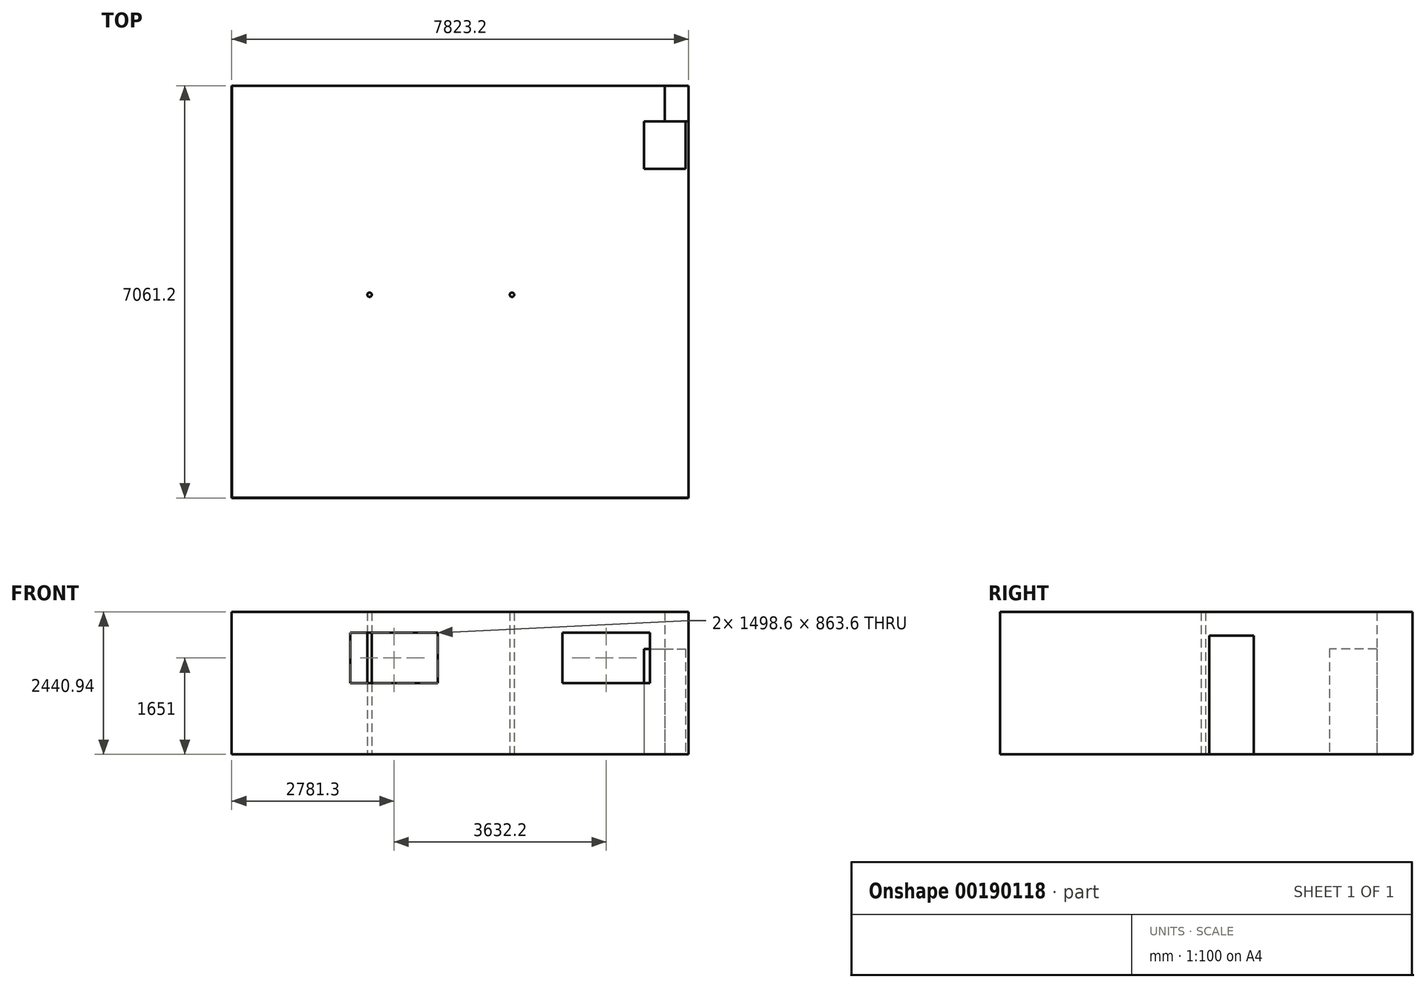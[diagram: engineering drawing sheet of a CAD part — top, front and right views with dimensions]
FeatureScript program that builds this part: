
annotation { "Feature Type Name" : "Feature", "Feature Type Description" : "" }
export const myFeature = defineFeature(function(context is Context, id is Id, definition is map)
    precondition{}
    {
        {
            var Q0;
            Q0=qCreatedBy(makeId("Top.planeOp"),FACE);
            var sketch = newSketch(context, id + "F0", { "sketchPlane" : qUnion([Q0])});
            skLineSegment(sketch, "E0.bottom", {"start": v(-3476.38, 3604.59) * mm, "end": v(4346.82, 3604.59) * mm});
            skLineSegment(sketch, "E0.top", {"start": v(-3476.38, -3456.61) * mm, "end": v(4346.82, -3456.61) * mm});
            skLineSegment(sketch, "E0.left", {"start": v(-3476.38, 3604.59) * mm, "end": v(-3476.38, -3456.61) * mm});
            skLineSegment(sketch, "E0.right", {"start": v(4346.82, 3604.59) * mm, "end": v(4346.82, -3456.61) * mm});
            skSolve(sketch);
        }
        {
            var Q0;
            Q0 = qSketchRegion(id + "F0", true);
            var Q1;
            Q1 = qConstructionFilter(qBodyType(qCreatedBy(id + "F0" ,EDGE), BodyType.WIRE), ConstructionObject.NO);
            extrude(context, id + "F1", {"entities" : qUnion([Q0]), "surfaceEntities" : qUnion([Q1]), "depth" : 2438.4 * mm});
        }
        {
            var Q0;
            Q0=makeQuery(id+"F1.opExtrude","CAP_FACE",FACE,{"disambiguationData":[OSD([sQuery(id+"F0.wireOp",EDGE,"E0.bottom"),sQuery(id+"F0.wireOp",EDGE,"E0.top"),sQuery(id+"F0.wireOp",EDGE,"E0.left"),sQuery(id+"F0.wireOp",EDGE,"E0.right")])],"isStart":false});
            shell(context, id + "F2", {"entities" : qUnion([Q0]), "thickness" : 2.54 * mm});
        }
        {
            var Q0;
            Q0=makeQuery(id+"F1.opExtrude","SWEPT_FACE",FACE,{"disambiguationData":[OSD([sQuery(id+"F0.wireOp",EDGE,"E0.top")])]});
            var sketch = newSketch(context, id + "F3", { "sketchPlane" : qUnion([Q0])});
            skLineSegment(sketch, "E1.bottom", {"start": v(3686.42, 2082.8) * mm, "end": v(2187.82, 2082.8) * mm});
            skLineSegment(sketch, "E1.top", {"start": v(3686.42, 1219.2) * mm, "end": v(2187.82, 1219.2) * mm});
            skLineSegment(sketch, "E1.left", {"start": v(3686.42, 2082.8) * mm, "end": v(3686.42, 1219.2) * mm});
            skLineSegment(sketch, "E1.right", {"start": v(2187.82, 2082.8) * mm, "end": v(2187.82, 1219.2) * mm});
            skLineSegment(sketch, "E2.bottom", {"start": v(54.22, 2082.8) * mm, "end": v(-1444.38, 2082.8) * mm});
            skLineSegment(sketch, "E2.top", {"start": v(54.22, 1219.2) * mm, "end": v(-1444.38, 1219.2) * mm});
            skLineSegment(sketch, "E2.left", {"start": v(54.22, 2082.8) * mm, "end": v(54.22, 1219.2) * mm});
            skLineSegment(sketch, "E2.right", {"start": v(-1444.38, 2082.8) * mm, "end": v(-1444.38, 1219.2) * mm});
            skSolve(sketch);
        }
        {
            var Q0;
            Q0=makeQuery(id+"F3.imprint","IMPRINT",FACE,{"disambiguationData":[TD([[makeQuery(id+"F3.imprint","IMPRINT",EDGE,{"derivedFrom":sQuery(id+"F3.wireOp",EDGE,"E2.bottom")}),1.0]])]});
            var Q1;
            Q1=makeQuery(id+"F3.imprint","IMPRINT",FACE,{"disambiguationData":[TD([[makeQuery(id+"F3.imprint","IMPRINT",EDGE,{"derivedFrom":sQuery(id+"F3.wireOp",EDGE,"E1.bottom")}),1.0]])]});
            extrude(context, id + "F4", {"entities" : qUnion([Q0, Q1]), "operationType" : NewBodyOperationType.REMOVE, "oppositeDirection" : true, "depth" : 2.54 * mm});
        }
        {
            var Q0;
            Q0=makeQuery(id+"F1.opExtrude","SWEPT_FACE",FACE,{"disambiguationData":[OSD([sQuery(id+"F0.wireOp",EDGE,"E0.right")])]});
            var sketch = newSketch(context, id + "F5", { "sketchPlane" : qUnion([Q0])});
            skLineSegment(sketch, "E3.bottom", {"start": v(886.79, 0) * mm, "end": v(124.79, 0) * mm});
            skLineSegment(sketch, "E3.top", {"start": v(886.79, 2032) * mm, "end": v(124.79, 2032) * mm});
            skLineSegment(sketch, "E3.left", {"start": v(886.79, 0) * mm, "end": v(886.79, 2032) * mm});
            skLineSegment(sketch, "E3.right", {"start": v(124.79, 0) * mm, "end": v(124.79, 2032) * mm});
            skSolve(sketch);
        }
        {
            var Q0;
            Q0=makeQuery(id+"F5.imprint","IMPRINT",FACE,{"disambiguationData":[TD([[makeQuery(id+"F5.imprint","IMPRINT",EDGE,{"derivedFrom":sQuery(id+"F5.wireOp",EDGE,"E3.bottom")}),-1.0]])]});
            extrude(context, id + "F6", {"entities" : qUnion([Q0]), "operationType" : NewBodyOperationType.REMOVE, "oppositeDirection" : true, "depth" : 2.54 * mm});
        }
        {
            var Q0;
            Q0=makeQuery(id+"F0.imprint","IMPRINT",FACE,{"disambiguationData":[TD([[makeQuery(id+"F0.imprint","IMPRINT",EDGE,{"derivedFrom":sQuery(id+"F0.wireOp",EDGE,"E0.bottom")}),-1.0]])]});
            var sketch = newSketch(context, id + "F7", { "sketchPlane" : qUnion([Q0])});
            skCircle(sketch, "E4", {"center": v(-1114.18, 23.19) * mm, "radius": 38.1 * mm});
            skCircle(sketch, "E5", {"center": v(1324.22, 23.19) * mm, "radius": 38.1 * mm});
            skSolve(sketch);
        }
        {
            var Q0;
            Q0 = qSketchRegion(id + "F7", true);
            extrude(context, id + "F8", {"entities" : qUnion([Q0]), "depth" : 2438.4 * mm});
        }
        {
            var Q0;
            Q0=makeQuery(id+"F2.opShell","OFFSET_FACE",FACE,{"disambiguationData":[OSD([sQuery(id+"F0.wireOp",EDGE,"E0.bottom"),sQuery(id+"F0.wireOp",EDGE,"E0.top"),sQuery(id+"F0.wireOp",EDGE,"E0.left"),sQuery(id+"F0.wireOp",EDGE,"E0.right")])]});
            var sketch = newSketch(context, id + "F9", { "sketchPlane" : qUnion([Q0])});
            skLineSegment(sketch, "E6.bottom", {"start": v(3937.88, 3602.05) * mm, "end": v(4344.28, 3602.05) * mm});
            skLineSegment(sketch, "E6.top", {"start": v(3937.88, 2992.45) * mm, "end": v(4344.28, 2992.45) * mm});
            skLineSegment(sketch, "E6.left", {"start": v(3937.88, 3602.05) * mm, "end": v(3937.88, 2992.45) * mm});
            skLineSegment(sketch, "E6.right", {"start": v(4344.28, 3602.05) * mm, "end": v(4344.28, 2992.45) * mm});
            skSolve(sketch);
        }
        {
            var Q0;
            Q0 = qSketchRegion(id + "F9", true);
            extrude(context, id + "F10", {"entities" : qUnion([Q0]), "depth" : 2438.4 * mm});
        }
        {
            var Q0;
            Q0=makeQuery(id+"F2.opShell","OFFSET_FACE",FACE,{"disambiguationData":[OSD([sQuery(id+"F0.wireOp",EDGE,"E0.bottom"),sQuery(id+"F0.wireOp",EDGE,"E0.top"),sQuery(id+"F0.wireOp",EDGE,"E0.left"),sQuery(id+"F0.wireOp",EDGE,"E0.right")])]});
            var sketch = newSketch(context, id + "F11", { "sketchPlane" : qUnion([Q0])});
            skLineSegment(sketch, "E7.bottom", {"start": v(3582.28, 2992.45) * mm, "end": v(4293.48, 2992.45) * mm});
            skLineSegment(sketch, "E7.top", {"start": v(3582.28, 2179.65) * mm, "end": v(4293.48, 2179.65) * mm});
            skLineSegment(sketch, "E7.left", {"start": v(3582.28, 2992.45) * mm, "end": v(3582.28, 2179.65) * mm});
            skLineSegment(sketch, "E7.right", {"start": v(4293.48, 2992.45) * mm, "end": v(4293.48, 2179.65) * mm});
            skSolve(sketch);
        }
        {
            var Q0;
            Q0=makeQuery(id+"F11.imprint","IMPRINT",FACE,{"disambiguationData":[TD([[makeQuery(id+"F11.imprint","IMPRINT",EDGE,{"derivedFrom":sQuery(id+"F11.wireOp",EDGE,"E7.bottom")}),-1.0]])]});
            extrude(context, id + "F12", {"entities" : qUnion([Q0]), "operationType" : NewBodyOperationType.ADD, "depth" : 1803.4 * mm});
        }
    });
